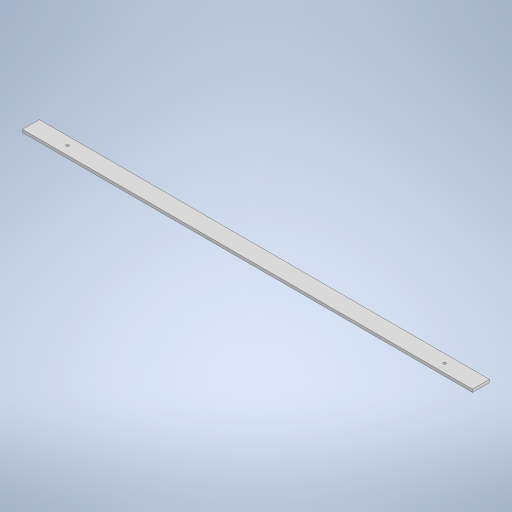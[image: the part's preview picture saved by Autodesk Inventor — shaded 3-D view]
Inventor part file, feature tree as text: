
AUTODESK INVENTOR PART (.ipt)
format: ipt  version: 2023 (Build 270158000, 158)  size: 241,152 bytes
history: native  units: in
note: dims shown in document units (in); Inventor stores cm internally (conversion verified against a paired STEP export)
features: sketch x1, extrude x1, hole x1
ambient origin geometry x8: Origin, YZ Plane, XZ Plane, XY Plane, X Axis, Y Axis, Z Axis, Center Point
bodies: Solid1 (feature_tree)
feature tree (3):
  sketch  "Sketch1"  dims[d0=40.0in d1=1.5in d2=0.25in d3=0.0in d4=3.24in d5=3.24in d6=0.25in d7=0.75in d8=0.375in d9=0.25in d10=0.5635in d11=1.0in d12=0.8108in]
  extrude  "Extrusion1"  Depth=1.5in
  hole  "Hole1"  [1 undecoded]
note: 1 required parameter value undecoded (feature->parameter linkage not recoverable at this tier; creation-order binding heuristic only, values carry confidence <= 0.55)
